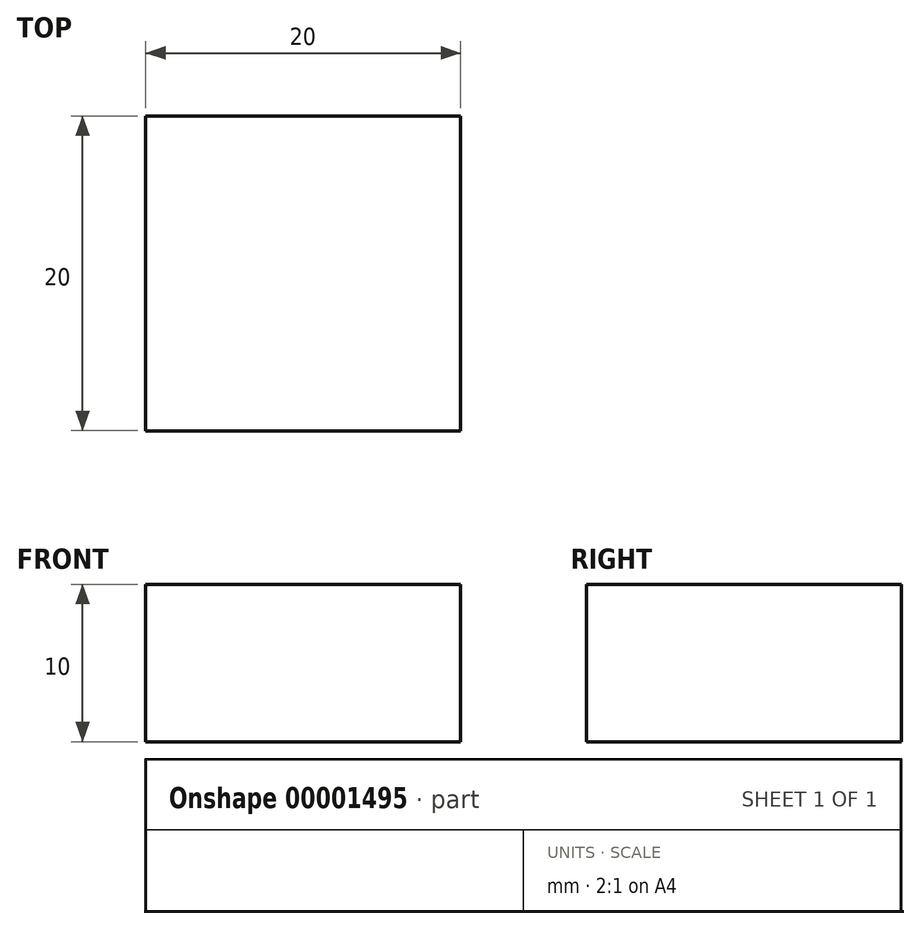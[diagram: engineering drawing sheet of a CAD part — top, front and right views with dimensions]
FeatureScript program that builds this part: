
annotation { "Feature Type Name" : "Feature", "Feature Type Description" : "" }
export const myFeature = defineFeature(function(context is Context, id is Id, definition is map)
    precondition{}
    {
        {
            var Q0;
            Q0=qCreatedBy(makeId("Top.planeOp"),FACE);
            var sketch = newSketch(context, id + "F0", { "sketchPlane" : qUnion([Q0])});
            skLineSegment(sketch, "E0.bottom", {"start": v(-10, 5.97) * mm, "end": v(10, 5.97) * mm});
            skLineSegment(sketch, "E0.top", {"start": v(-10, -14.03) * mm, "end": v(10, -14.03) * mm});
            skLineSegment(sketch, "E0.left", {"start": v(-10, 5.97) * mm, "end": v(-10, -14.03) * mm});
            skLineSegment(sketch, "E0.right", {"start": v(10, 5.97) * mm, "end": v(10, -14.03) * mm});
            skSolve(sketch);
        }
        {
            var Q0;
            Q0=makeQuery(id+"F0.imprint","IMPRINT",FACE,{"disambiguationData":[TD([[makeQuery(id+"F0.imprint","IMPRINT",EDGE,{"derivedFrom":sQuery(id+"F0.wireOp",EDGE,"E0.bottom")}),-1.0]])]});
            extrude(context, id + "F1", {"entities" : qUnion([Q0]), "depth" : 10 * mm});
        }
    });
